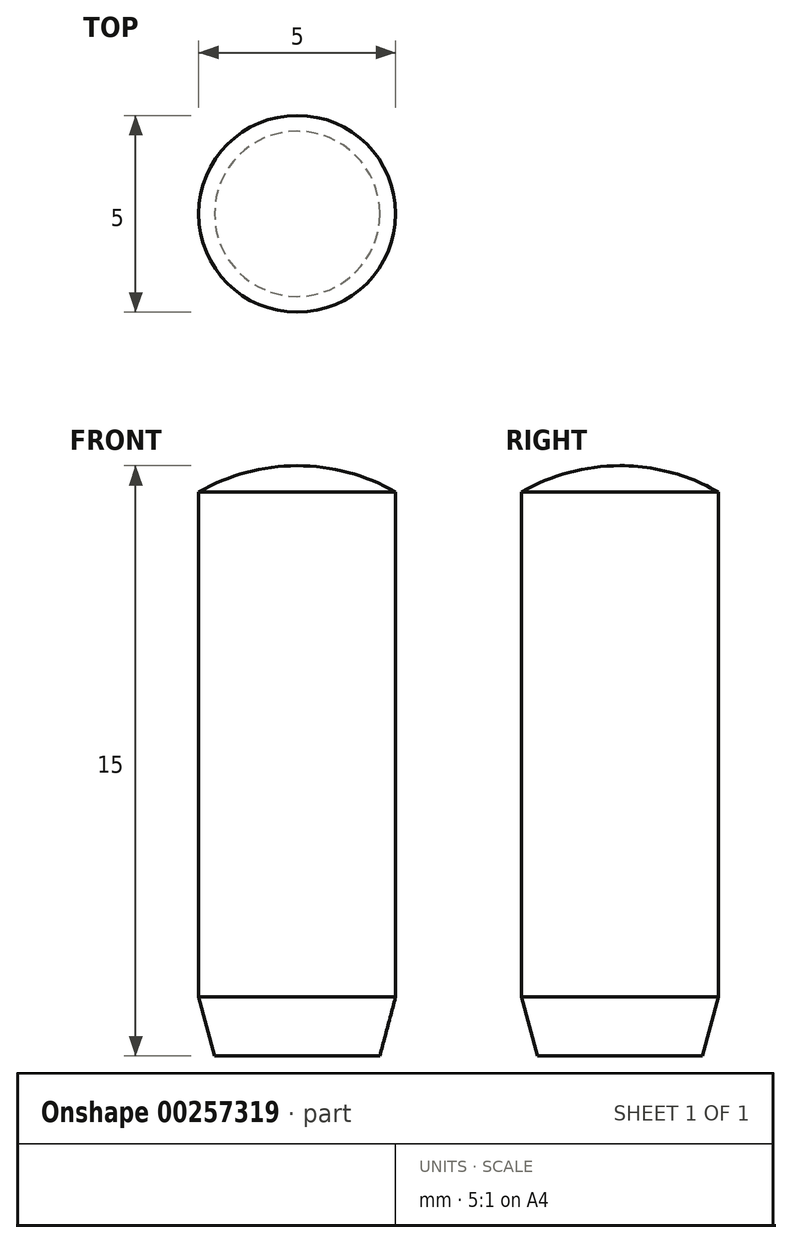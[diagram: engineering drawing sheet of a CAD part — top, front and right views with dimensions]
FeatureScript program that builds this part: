
annotation { "Feature Type Name" : "Feature", "Feature Type Description" : "" }
export const myFeature = defineFeature(function(context is Context, id is Id, definition is map)
    precondition{}
    {
        {
            var Q0;
            Q0=qCreatedBy(makeId("Right.planeOp"),FACE);
            var sketch = newSketch(context, id + "F0", { "sketchPlane" : qUnion([Q0])});
            skLineSegment(sketch, "E0", {"start": v(2.1, 0) * mm, "end": v(2.5, 1.5) * mm});
            skLineSegment(sketch, "E1", {"start": v(2.5, 1.5) * mm, "end": v(2.5, 14.33) * mm});
            skLineSegment(sketch, "E2", {"start": v(0, 15) * mm, "end": v(0, 0) * mm});
            skLineSegment(sketch, "E3", {"start": v(0, 0) * mm, "end": v(2.1, 0) * mm});
            skLineSegment(sketch, "E4", {"start": v(0, 19.34) * mm, "end": v(0, -3.59) * mm, "construction": true});
            skArc(sketch, "E5.trimOffspring", {"start": v(2.5, 14.33) * mm, "mid": v(1.3, 14.83) * mm, "end": v(0, 15) * mm});
            skSolve(sketch);
        }
        {
            var Q0;
            Q0=makeQuery(id+"F0.imprint","IMPRINT",FACE,{"disambiguationData":[TD([[makeQuery(id+"F0.imprint","IMPRINT",EDGE,{"derivedFrom":sQuery(id+"F0.wireOp",EDGE,"E0")}),1.0]])]});
            var Q1;
            Q1=sQuery(id+"F0.wireOp",EDGE,"E4");
            revolve(context, id + "F1", {"entities" : qUnion([Q0]), "axis" : qUnion([Q1]), "revolveType" : RevolveType.FULL});
        }
    });
